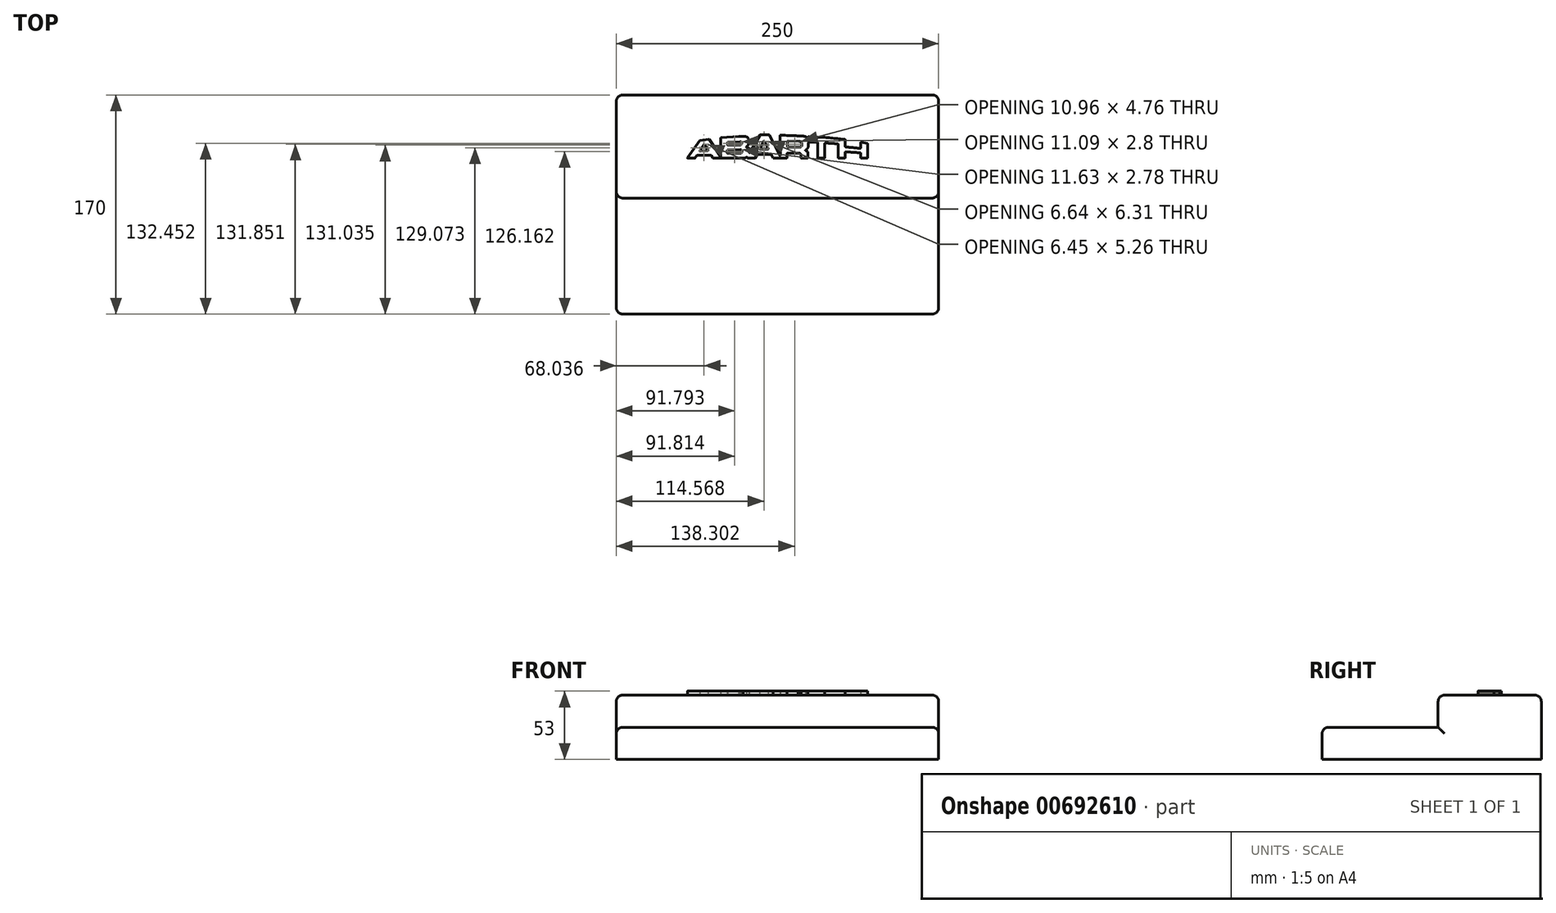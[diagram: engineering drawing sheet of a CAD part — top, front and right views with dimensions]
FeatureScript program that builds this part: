
annotation { "Feature Type Name" : "Feature", "Feature Type Description" : "" }
export const myFeature = defineFeature(function(context is Context, id is Id, definition is map)
    precondition{}
    {
        {
            var Q0;
            Q0=qCreatedBy(makeId("Top.planeOp"),FACE);
            var sketch = newSketch(context, id + "F0", { "sketchPlane" : qUnion([Q0])});
            skLineSegment(sketch, "E0.bottom", {"start": v(125, -40) * mm, "end": v(-125, -40) * mm});
            skLineSegment(sketch, "E0.top", {"start": v(125, 40) * mm, "end": v(-125, 40) * mm});
            skLineSegment(sketch, "E0.left", {"start": v(125, -40) * mm, "end": v(125, 40) * mm});
            skLineSegment(sketch, "E0.right", {"start": v(-125, -40) * mm, "end": v(-125, 40) * mm});
            skPoint(sketch, "E0.middle", {"position": v(0, 0) * mm});
            skSolve(sketch);
        }
        {
            var Q0;
            Q0=makeQuery(id+"F0.imprint","IMPRINT",FACE,{"disambiguationData":[TD([[makeQuery(id+"F0.imprint","IMPRINT",EDGE,{"derivedFrom":sQuery(id+"F0.wireOp",EDGE,"E0.bottom")}),-1.0]])]});
            extrude(context, id + "F1", {"entities" : qUnion([Q0]), "depth" : 25 * mm, "offsetDistance" : 25 * mm});
        }
        {
            var Q0;
            Q0=makeQuery(id+"F1.opExtrude","CAP_FACE",FACE,{"disambiguationData":[OSD([sQuery(id+"F0.wireOp",EDGE,"E0.bottom"),sQuery(id+"F0.wireOp",EDGE,"E0.top"),sQuery(id+"F0.wireOp",EDGE,"E0.left"),sQuery(id+"F0.wireOp",EDGE,"E0.right")])],"isStart":false});
            var sketch = newSketch(context, id + "F2", { "sketchPlane" : qUnion([Q0])});
            skLineSegment(sketch, "E1", {"start": v(-69.64, -9.06) * mm, "end": v(-64.06, -9.06) * mm});
            skLineSegment(sketch, "E2", {"start": v(-63.89, -8.97) * mm, "end": v(-62.5, -6.84) * mm});
            skLineSegment(sketch, "E3", {"start": v(-62.33, -6.75) * mm, "end": v(-51.48, -6.75) * mm});
            skLineSegment(sketch, "E4", {"start": v(-51.3, -6.84) * mm, "end": v(-50.02, -8.94) * mm});
            skLineSegment(sketch, "E5", {"start": v(-49.85, -9.04) * mm, "end": v(-26.5, -9) * mm});
            skLineSegment(sketch, "E6", {"start": v(-23.3, -8.96) * mm, "end": v(-17.46, -9.05) * mm});
            skLineSegment(sketch, "E7", {"start": v(-17.28, -8.95) * mm, "end": v(-15.84, -6.3) * mm});
            skLineSegment(sketch, "E8", {"start": v(-15.75, -6.24) * mm, "end": v(-4.93, -6.24) * mm});
            skLineSegment(sketch, "E9", {"start": v(-4.75, -6.35) * mm, "end": v(-3.41, -9) * mm});
            skLineSegment(sketch, "E10", {"start": v(-3.41, -9) * mm, "end": v(7.3, -8.99) * mm});
            skLineSegment(sketch, "E11", {"start": v(7.5, -8.79) * mm, "end": v(7.49, -5.27) * mm});
            skLineSegment(sketch, "E12", {"start": v(7.69, -5.07) * mm, "end": v(15.94, -5.07) * mm});
            skLineSegment(sketch, "E13", {"start": v(18.18, -6.73) * mm, "end": v(18.18, -8.82) * mm});
            skLineSegment(sketch, "E14", {"start": v(18.38, -9.02) * mm, "end": v(23.46, -9.02) * mm});
            skLineSegment(sketch, "E15", {"start": v(23.66, -8.82) * mm, "end": v(23.66, -5.07) * mm});
            skLineSegment(sketch, "E16", {"start": v(31.26, 3.12) * mm, "end": v(31.26, -8.71) * mm});
            skLineSegment(sketch, "E17", {"start": v(31.46, -8.91) * mm, "end": v(36.56, -8.91) * mm});
            skLineSegment(sketch, "E18", {"start": v(36.76, -8.71) * mm, "end": v(36.76, 2.47) * mm});
            skLineSegment(sketch, "E19", {"start": v(47.1, 1.82) * mm, "end": v(47.11, -8.74) * mm});
            skLineSegment(sketch, "E20", {"start": v(47.31, -8.94) * mm, "end": v(52.37, -8.94) * mm});
            skLineSegment(sketch, "E21", {"start": v(52.57, -8.74) * mm, "end": v(52.57, -4.38) * mm});
            skLineSegment(sketch, "E22", {"start": v(64.52, -5.17) * mm, "end": v(64.53, -8.78) * mm});
            skLineSegment(sketch, "E23", {"start": v(64.73, -8.98) * mm, "end": v(69.68, -8.98) * mm});
            skLineSegment(sketch, "E24", {"start": v(69.88, -8.78) * mm, "end": v(69.88, 2.26) * mm});
            skLineSegment(sketch, "E25", {"start": v(69.7, 2.46) * mm, "end": v(64.77, 3.25) * mm});
            skLineSegment(sketch, "E26", {"start": v(64.54, 3.05) * mm, "end": v(64.54, -1.3) * mm});
            skLineSegment(sketch, "E27", {"start": v(52.64, -0.15) * mm, "end": v(52.64, 5.27) * mm});
            skPoint(sketch, "E28.1.internal.snap0", {"position": v(58.57, -0.93) * mm});
            skFitSpline(sketch, "E28", {"points": [v(52.75, -0.34) * mm, v(59.5, -0.93) * mm, v(64.4, -1.5) * mm], "startDerivative": vector(13.02, -1.03) * mm, "endDerivative": vector(10.2, -1.3) * mm});
            skFitSpline(sketch, "E29", {"points": [v(64.42, -4.98) * mm, v(60.34, -4.58) * mm, v(55.98, -4.34) * mm, v(52.7, -4.18) * mm], "startDerivative": vector(-11.7, 1.26) * mm, "endDerivative": vector(-10.29, 0.51) * mm});
            skFitSpline(sketch, "E30", {"points": [v(36.88, 2.68) * mm, v(42.24, 2.46) * mm, v(47, 2.01) * mm], "startDerivative": vector(10.58, -0.3) * mm, "endDerivative": vector(9.64, -1.04) * mm});
            skFitSpline(sketch, "E31", {"points": [v(52.52, 5.46) * mm, v(38.45, 6.9) * mm, v(23.98, 7.7) * mm], "startDerivative": vector(-28.22, 3.11) * mm, "endDerivative": vector(-28.88, 1.38) * mm});
            skLineSegment(sketch, "E32", {"start": v(24.28, 3.32) * mm, "end": v(31.06, 3.32) * mm});
            skLineSegment(sketch, "E33", {"start": v(-6.23, 8.9) * mm, "end": v(1.9, -7.08) * mm});
            skLineSegment(sketch, "E34", {"start": v(2.07, 8.37) * mm, "end": v(2.27, -6.99) * mm});
            skLineSegment(sketch, "E35", {"start": v(-13.5, 9.02) * mm, "end": v(-6.4, 9) * mm});
            skLineSegment(sketch, "E36", {"start": v(-13.68, 8.92) * mm, "end": v(-21.48, -4.95) * mm});
            skLineSegment(sketch, "E37", {"start": v(-69.8, -8.74) * mm, "end": v(-60.27, 4.59) * mm});
            skLineSegment(sketch, "E38", {"start": v(-60.13, 4.67) * mm, "end": v(-53.17, 5.56) * mm});
            skLineSegment(sketch, "E39", {"start": v(-52.98, 5.47) * mm, "end": v(-44.42, -7.51) * mm});
            skLineSegment(sketch, "E40", {"start": v(-44.05, -7.4) * mm, "end": v(-44.05, 6.67) * mm});
            skLineSegment(sketch, "E41", {"start": v(-43.87, 6.87) * mm, "end": v(-30.13, 7.83) * mm});
            skLineSegment(sketch, "E42", {"start": v(-23.5, -8.77) * mm, "end": v(-23.5, -8.37) * mm});
            skFitSpline(sketch, "E43", {"points": [v(-23.7, -8.13) * mm, v(-24.5, -8.62) * mm, v(-25.52, -8.94) * mm, v(-26.5, -9) * mm], "startDerivative": vector(-2.31, -1.62) * mm, "endDerivative": vector(-2.91, -0.1) * mm});
            skFitSpline(sketch, "E44", {"points": [v(-21.67, -5.2) * mm, v(-21.66, -3.24) * mm, v(-21.74, -2.03) * mm, v(-22.12, -1.33) * mm, v(-23.2, -0.73) * mm, v(-24.06, -0.6) * mm], "startDerivative": vector(0.06, 7.93) * mm, "endDerivative": vector(-4.73, 0.3) * mm});
            skFitSpline(sketch, "E45", {"points": [v(-24.13, -0.1) * mm, v(-23.14, 0.54) * mm, v(-22.14, 2.46) * mm, v(-22.12, 4.53) * mm, v(-22.65, 6.42) * mm, v(-23.83, 7.5) * mm, v(-25.3, 7.9) * mm, v(-28.37, 7.93) * mm, v(-30.13, 7.83) * mm], "startDerivative": vector(10.17, 4.79) * mm, "endDerivative": vector(-13.04, -0.76) * mm});
            skFitSpline(sketch, "E46", {"points": [v(2.4, 8.78) * mm, v(16.04, 8.3) * mm, v(20.13, 8.07) * mm, v(22.39, 7.37) * mm, v(23.23, 6.73) * mm, v(23.65, 6.14) * mm], "startDerivative": vector(38.58, -1.46) * mm, "endDerivative": vector(4.08, -6.44) * mm});
            skFitSpline(sketch, "E47", {"points": [v(24.08, 3.2) * mm, v(24, 0.71) * mm, v(23.66, -0.8) * mm, v(22.61, -2.27) * mm, v(21.75, -2.78) * mm], "startDerivative": vector(-0.22, -8.68) * mm, "endDerivative": vector(-4.38, -1.91) * mm});
            skFitSpline(sketch, "E48", {"points": [v(18.18, -6.73) * mm, v(18.07, -5.9) * mm, v(17.47, -5.26) * mm, v(16.6, -5.1) * mm, v(15.94, -5.07) * mm], "startDerivative": vector(0, 3.34) * mm, "endDerivative": vector(-2.8, 0.11) * mm});
            skFitSpline(sketch, "E49", {"points": [v(23.66, -5.07) * mm, v(23.6, -4.53) * mm, v(23.33, -4) * mm, v(22.8, -3.56) * mm, v(22, -3.3) * mm, v(21.8, -3.27) * mm], "startDerivative": vector(-0.2, 2.72) * mm, "endDerivative": vector(-1.34, 0.14) * mm});
            skLineSegment(sketch, "E50", {"start": v(23.85, 7.5) * mm, "end": v(23.88, 6.47) * mm});
            skArc(sketch, "E51.filletArc", {"start": v(-69.8, -8.74) * mm, "mid": v(-69.82, -8.95) * mm, "end": v(-69.64, -9.06) * mm});
            skArc(sketch, "E52.filletArc", {"start": v(-64.06, -9.06) * mm, "mid": v(-63.96, -9.03) * mm, "end": v(-63.89, -8.97) * mm});
            skArc(sketch, "E53.filletArc", {"start": v(-62.33, -6.75) * mm, "mid": v(-62.42, -6.77) * mm, "end": v(-62.5, -6.84) * mm});
            skArc(sketch, "E54.filletArc", {"start": v(-51.3, -6.84) * mm, "mid": v(-51.38, -6.77) * mm, "end": v(-51.48, -6.75) * mm});
            skArc(sketch, "E55.filletArc", {"start": v(-50.02, -8.94) * mm, "mid": v(-49.95, -9.01) * mm, "end": v(-49.85, -9.04) * mm});
            skArc(sketch, "E56.filletArc", {"start": v(-52.98, 5.47) * mm, "mid": v(-53.06, 5.54) * mm, "end": v(-53.17, 5.56) * mm});
            skPoint(sketch, "E57.visualSharp", {"position": v(-60.22, 4.66) * mm});
            skArc(sketch, "E57.filletArc", {"start": v(-60.13, 4.67) * mm, "mid": v(-60.2, 4.64) * mm, "end": v(-60.27, 4.59) * mm});
            skArc(sketch, "E58.filletArc", {"start": v(-43.87, 6.87) * mm, "mid": v(-44, 6.8) * mm, "end": v(-44.05, 6.67) * mm});
            skArc(sketch, "E59.filletArc", {"start": v(-17.46, -9.05) * mm, "mid": v(-17.36, -9.02) * mm, "end": v(-17.28, -8.95) * mm});
            skArc(sketch, "E60.filletArc", {"start": v(-23.5, -8.77) * mm, "mid": v(-23.44, -8.9) * mm, "end": v(-23.3, -8.96) * mm});
            skArc(sketch, "E61.filletArc", {"start": v(-15.75, -6.24) * mm, "mid": v(-15.8, -6.25) * mm, "end": v(-15.84, -6.3) * mm});
            skArc(sketch, "E62.filletArc", {"start": v(-4.75, -6.35) * mm, "mid": v(-4.82, -6.27) * mm, "end": v(-4.93, -6.24) * mm});
            skArc(sketch, "E63.filletArc", {"start": v(7.3, -8.99) * mm, "mid": v(7.44, -8.93) * mm, "end": v(7.5, -8.79) * mm});
            skArc(sketch, "E64.filletArc", {"start": v(7.69, -5.07) * mm, "mid": v(7.55, -5.13) * mm, "end": v(7.49, -5.27) * mm});
            skArc(sketch, "E65.filletArc", {"start": v(18.18, -8.82) * mm, "mid": v(18.24, -8.96) * mm, "end": v(18.38, -9.02) * mm});
            skArc(sketch, "E66.filletArc", {"start": v(23.46, -9.02) * mm, "mid": v(23.6, -8.96) * mm, "end": v(23.66, -8.82) * mm});
            skArc(sketch, "E67.filletArc", {"start": v(24.28, 3.32) * mm, "mid": v(24.14, 3.26) * mm, "end": v(24.08, 3.12) * mm});
            skArc(sketch, "E68.filletArc", {"start": v(31.26, 3.12) * mm, "mid": v(31.2, 3.26) * mm, "end": v(31.06, 3.32) * mm});
            skArc(sketch, "E69.filletArc", {"start": v(31.26, -8.71) * mm, "mid": v(31.32, -8.85) * mm, "end": v(31.46, -8.91) * mm});
            skArc(sketch, "E70.filletArc", {"start": v(36.56, -8.91) * mm, "mid": v(36.7, -8.85) * mm, "end": v(36.76, -8.71) * mm});
            skArc(sketch, "E71.filletArc", {"start": v(36.96, 2.67) * mm, "mid": v(36.82, 2.62) * mm, "end": v(36.76, 2.47) * mm});
            skArc(sketch, "E72.filletArc", {"start": v(47.1, 1.82) * mm, "mid": v(47.05, 1.95) * mm, "end": v(46.93, 2.02) * mm});
            skArc(sketch, "E73.filletArc", {"start": v(47.11, -8.74) * mm, "mid": v(47.17, -8.89) * mm, "end": v(47.31, -8.94) * mm});
            skArc(sketch, "E74.filletArc", {"start": v(52.37, -8.94) * mm, "mid": v(52.51, -8.89) * mm, "end": v(52.57, -8.74) * mm});
            skArc(sketch, "E75.filletArc", {"start": v(52.78, -4.18) * mm, "mid": v(52.64, -4.24) * mm, "end": v(52.57, -4.38) * mm});
            skArc(sketch, "E76.filletArc", {"start": v(64.53, -8.78) * mm, "mid": v(64.59, -8.92) * mm, "end": v(64.73, -8.98) * mm});
            skArc(sketch, "E77.filletArc", {"start": v(64.52, -5.17) * mm, "mid": v(64.47, -5.04) * mm, "end": v(64.35, -4.97) * mm});
            skArc(sketch, "E78.filletArc", {"start": v(69.68, -8.98) * mm, "mid": v(69.82, -8.92) * mm, "end": v(69.88, -8.78) * mm});
            skArc(sketch, "E79.filletArc", {"start": v(69.88, 2.26) * mm, "mid": v(69.83, 2.39) * mm, "end": v(69.7, 2.46) * mm});
            skArc(sketch, "E80.filletArc", {"start": v(64.77, 3.25) * mm, "mid": v(64.6, 3.2) * mm, "end": v(64.54, 3.05) * mm});
            skArc(sketch, "E81.filletArc", {"start": v(64.31, -1.5) * mm, "mid": v(64.47, -1.45) * mm, "end": v(64.54, -1.3) * mm});
            skArc(sketch, "E82.filletArc", {"start": v(52.64, -0.15) * mm, "mid": v(52.69, -0.29) * mm, "end": v(52.82, -0.35) * mm});
            skArc(sketch, "E83.filletArc", {"start": v(52.64, 5.27) * mm, "mid": v(52.59, 5.4) * mm, "end": v(52.46, 5.47) * mm});
            skArc(sketch, "E84.filletArc", {"start": v(24.06, 7.7) * mm, "mid": v(23.9, 7.65) * mm, "end": v(23.85, 7.5) * mm});
            skArc(sketch, "E85.filletArc", {"start": v(2.48, 8.78) * mm, "mid": v(2.19, 8.66) * mm, "end": v(2.07, 8.37) * mm});
            skPoint(sketch, "E86.visualSharp", {"position": v(-6.28, 9) * mm});
            skArc(sketch, "E86.filletArc", {"start": v(-6.23, 8.9) * mm, "mid": v(-6.3, 8.97) * mm, "end": v(-6.4, 9) * mm});
            skArc(sketch, "E87.filletArc", {"start": v(-13.5, 9.02) * mm, "mid": v(-13.6, 9) * mm, "end": v(-13.68, 8.92) * mm});
            skArc(sketch, "E88.filletArc", {"start": v(-44.42, -7.51) * mm, "mid": v(-44.2, -7.6) * mm, "end": v(-44.05, -7.4) * mm});
            skArc(sketch, "E89.filletArc", {"start": v(-21.67, -4.9) * mm, "mid": v(-21.6, -5) * mm, "end": v(-21.48, -4.95) * mm});
            skArc(sketch, "E90.filletArc", {"start": v(1.9, -7.08) * mm, "mid": v(2.12, -7.18) * mm, "end": v(2.27, -6.99) * mm});
            skArc(sketch, "E91.filletArc", {"start": v(-23.5, -8.37) * mm, "mid": v(-23.61, -8.2) * mm, "end": v(-23.82, -8.2) * mm});
            skArc(sketch, "E92.filletArc", {"start": v(23.51, 6.35) * mm, "mid": v(23.74, 6.27) * mm, "end": v(23.88, 6.47) * mm});
            skArc(sketch, "E93.filletArc", {"start": v(-23.93, -0.01) * mm, "mid": v(-24.1, -0.36) * mm, "end": v(-23.82, -0.61) * mm});
            skArc(sketch, "E94.filletArc", {"start": v(21.93, -2.7) * mm, "mid": v(21.75, -3.02) * mm, "end": v(22, -3.3) * mm});
            skLineSegment(sketch, "E95", {"start": v(-59.98, -3.56) * mm, "end": v(-53.93, -3.28) * mm});
            skLineSegment(sketch, "E96", {"start": v(-53.77, -2.97) * mm, "end": v(-56.66, 1.61) * mm});
            skLineSegment(sketch, "E97", {"start": v(-57, 1.61) * mm, "end": v(-60.16, -3.25) * mm});
            skLineSegment(sketch, "E98", {"start": v(-13.55, -2.12) * mm, "end": v(-7.31, -2.12) * mm});
            skLineSegment(sketch, "E99", {"start": v(-7.14, -1.83) * mm, "end": v(-10.08, 4.08) * mm});
            skLineSegment(sketch, "E100", {"start": v(-10.43, 4.09) * mm, "end": v(-13.72, -1.82) * mm});
            skLineSegment(sketch, "E101", {"start": v(7.82, 4.03) * mm, "end": v(7.82, -0.23) * mm});
            skLineSegment(sketch, "E102", {"start": v(8.02, -0.43) * mm, "end": v(16.64, -0.53) * mm});
            skLineSegment(sketch, "E103", {"start": v(16.49, 4.03) * mm, "end": v(8.03, 4.23) * mm});
            skLineSegment(sketch, "E104", {"start": v(18.78, 2.1) * mm, "end": v(18.78, 0.85) * mm});
            skFitSpline(sketch, "E105", {"points": [v(16.49, 4.03) * mm, v(17.65, 3.85) * mm, v(18.44, 3.3) * mm, v(18.76, 2.56) * mm, v(18.78, 2.1) * mm], "startDerivative": vector(4.08, -0.25) * mm, "endDerivative": vector(-0.06, -2.33) * mm});
            skFitSpline(sketch, "E106", {"points": [v(18.78, 0.85) * mm, v(18.75, 0.44) * mm, v(18.34, -0.14) * mm, v(17.52, -0.48) * mm, v(16.64, -0.53) * mm], "startDerivative": vector(0.06, -2.04) * mm, "endDerivative": vector(-3.14, 0) * mm});
            skLineSegment(sketch, "E107", {"start": v(-38.67, 3.2) * mm, "end": v(-38.75, 1.26) * mm});
            skLineSegment(sketch, "E108", {"start": v(-38.48, 3.4) * mm, "end": v(-29.2, 3.85) * mm});
            skLineSegment(sketch, "E109", {"start": v(-29.17, 1.19) * mm, "end": v(-38.55, 1.05) * mm});
            skLineSegment(sketch, "E110", {"start": v(-28.93, -2.45) * mm, "end": v(-38.73, -2.79) * mm});
            skLineSegment(sketch, "E111", {"start": v(-28.99, -5.23) * mm, "end": v(-38.8, -5.21) * mm});
            skFitSpline(sketch, "E112", {"points": [v(-29.2, 3.85) * mm, v(-28.27, 3.74) * mm, v(-27.78, 3.28) * mm, v(-27.64, 2.65) * mm, v(-27.8, 1.95) * mm, v(-28.19, 1.46) * mm, v(-28.54, 1.24) * mm, v(-28.87, 1.19) * mm, v(-29.17, 1.19) * mm], "startDerivative": vector(6.28, 0.05) * mm, "endDerivative": vector(-3.3, 0.32) * mm});
            skFitSpline(sketch, "E113", {"points": [v(-28.99, -5.23) * mm, v(-28.29, -5.18) * mm, v(-27.72, -4.7) * mm, v(-27.37, -3.67) * mm, v(-27.75, -2.83) * mm, v(-28.4, -2.5) * mm, v(-28.93, -2.45) * mm], "startDerivative": vector(4.62, -0.21) * mm, "endDerivative": vector(-3.8, 0.08) * mm});
            skLineSegment(sketch, "E114.trimOffspring", {"start": v(-38.92, -2.98) * mm, "end": v(-39, -5) * mm});
            skPoint(sketch, "E115.visualSharp", {"position": v(-56.82, 1.87) * mm});
            skArc(sketch, "E115.filletArc", {"start": v(-56.66, 1.61) * mm, "mid": v(-56.82, 1.7) * mm, "end": v(-57, 1.61) * mm});
            skPoint(sketch, "E116.visualSharp", {"position": v(-53.58, -3.26) * mm});
            skArc(sketch, "E116.filletArc", {"start": v(-53.93, -3.28) * mm, "mid": v(-53.76, -3.17) * mm, "end": v(-53.77, -2.97) * mm});
            skPoint(sketch, "E117.visualSharp", {"position": v(-60.37, -3.58) * mm});
            skArc(sketch, "E117.filletArc", {"start": v(-60.16, -3.25) * mm, "mid": v(-60.16, -3.46) * mm, "end": v(-59.98, -3.56) * mm});
            skPoint(sketch, "E118.visualSharp", {"position": v(-10.25, 4.42) * mm});
            skArc(sketch, "E118.filletArc", {"start": v(-10.08, 4.08) * mm, "mid": v(-10.25, 4.19) * mm, "end": v(-10.43, 4.09) * mm});
            skPoint(sketch, "E119.visualSharp", {"position": v(-13.9, -2.12) * mm});
            skArc(sketch, "E119.filletArc", {"start": v(-13.72, -1.82) * mm, "mid": v(-13.72, -2.02) * mm, "end": v(-13.55, -2.12) * mm});
            skPoint(sketch, "E120.visualSharp", {"position": v(-7, -2.12) * mm});
            skArc(sketch, "E120.filletArc", {"start": v(-7.31, -2.12) * mm, "mid": v(-7.14, -2.02) * mm, "end": v(-7.14, -1.83) * mm});
            skPoint(sketch, "E121.visualSharp", {"position": v(7.82, 4.24) * mm});
            skArc(sketch, "E121.filletArc", {"start": v(8.03, 4.23) * mm, "mid": v(7.88, 4.17) * mm, "end": v(7.82, 4.03) * mm});
            skPoint(sketch, "E122.visualSharp", {"position": v(7.82, -0.42) * mm});
            skArc(sketch, "E122.filletArc", {"start": v(7.82, -0.23) * mm, "mid": v(7.88, -0.37) * mm, "end": v(8.02, -0.43) * mm});
            skPoint(sketch, "E123.visualSharp", {"position": v(-38.67, 3.4) * mm});
            skArc(sketch, "E123.filletArc", {"start": v(-38.48, 3.4) * mm, "mid": v(-38.61, 3.34) * mm, "end": v(-38.67, 3.2) * mm});
            skPoint(sketch, "E124.visualSharp", {"position": v(-38.76, 1.05) * mm});
            skArc(sketch, "E124.filletArc", {"start": v(-38.75, 1.26) * mm, "mid": v(-38.7, 1.12) * mm, "end": v(-38.55, 1.05) * mm});
            skPoint(sketch, "E125.visualSharp", {"position": v(-38.91, -2.8) * mm});
            skArc(sketch, "E125.filletArc", {"start": v(-38.73, -2.79) * mm, "mid": v(-38.86, -2.84) * mm, "end": v(-38.92, -2.98) * mm});
            skPoint(sketch, "E126.visualSharp", {"position": v(-39, -5.21) * mm});
            skArc(sketch, "E126.filletArc", {"start": v(-39, -5) * mm, "mid": v(-38.94, -5.15) * mm, "end": v(-38.8, -5.21) * mm});
            skLineSegment(sketch, "E127", {"start": v(-81, 0) * mm, "end": v(81, 0) * mm, "construction": true});
            skLineSegment(sketch, "E128", {"start": v(0, 13.76) * mm, "end": v(0, -13.76) * mm, "construction": true});
            skPoint(sketch, "E129.middle", {"position": v(0, 0) * mm});
            skSolve(sketch);
        }
        {
            var Q0;
            Q0=qSketchRegion(id+"F2",true);
            extrude(context, id + "F3", {"entities" : qUnion([Q0]), "depth" : 3 * mm, "offsetDistance" : 25 * mm});
        }
        {
            var Q0;
            Q0=makeQuery(id+"F1.opExtrude","CAP_FACE",FACE,{"disambiguationData":[OSD([sQuery(id+"F0.wireOp",EDGE,"E0.bottom"),sQuery(id+"F0.wireOp",EDGE,"E0.top"),sQuery(id+"F0.wireOp",EDGE,"E0.left"),sQuery(id+"F0.wireOp",EDGE,"E0.right")])],"isStart":true});
            var sketch = newSketch(context, id + "F4", { "sketchPlane" : qUnion([Q0])});
            skLineSegment(sketch, "E130.bottom", {"start": v(-125, -40) * mm, "end": v(125, -40) * mm});
            skLineSegment(sketch, "E130.top", {"start": v(-125, 130) * mm, "end": v(125, 130) * mm});
            skLineSegment(sketch, "E130.left", {"start": v(-125, -40) * mm, "end": v(-125, 130) * mm});
            skLineSegment(sketch, "E130.right", {"start": v(125, -40) * mm, "end": v(125, 130) * mm});
            skSolve(sketch);
        }
        {
            var Q0;
            {var subQ0=sQuery(id+"F4.wireOp",EDGE,"E130.top");Q0=makeQuery(id+"F4.imprint","IMPRINT",FACE,{"disambiguationData":[TD([[makeQuery(id+"F4.imprint","IMPRINT",EDGE,{"derivedFrom":subQ0}),-1.0]])]});}
            var Q1;
            {var subQ0=sQuery(id+"F4.wireOp",EDGE,"E130.bottom");Q1=makeQuery(id+"F4.imprint","IMPRINT",FACE,{"disambiguationData":[TD([[makeQuery(id+"F4.imprint","IMPRINT",EDGE,{"derivedFrom":subQ0}),-1.0]])]});}
            extrude(context, id + "F5", {"entities" : qUnion([Q0, Q1]), "operationType" : NewBodyOperationType.ADD, "depth" : 25 * mm, "offsetDistance" : 25 * mm});
        }
        {
            var Q0;
            Q0=makeQuery(id+"F1.opExtrude","CAP_EDGE",EDGE,{"disambiguationData":[OSD([sQuery(id+"F0.wireOp",EDGE,"E0.bottom")])],"isStart":false});
            var Q1;
            Q1=makeQuery(id+"F1.opExtrude","CAP_EDGE",EDGE,{"disambiguationData":[OSD([sQuery(id+"F0.wireOp",EDGE,"E0.left")])],"isStart":false});
            var Q2;
            Q2=makeQuery(id+"F1.opExtrude","CAP_EDGE",EDGE,{"disambiguationData":[OSD([sQuery(id+"F0.wireOp",EDGE,"E0.right")])],"isStart":false});
            var Q3;
            Q3=makeQuery(id+"F1.opExtrude","CAP_EDGE",EDGE,{"disambiguationData":[OSD([sQuery(id+"F0.wireOp",EDGE,"E0.top")])],"isStart":false});
            var Q4;
            Q4=makeQuery(id+"F5.boolean.opBoolean","MERGE",EDGE,{"derivedFrom":[makeQuery(id+"F1.opExtrude","SWEPT_EDGE",EDGE,{"disambiguationData":[OSD([sQuery(id+"F0.wireOp",EDGE,"E0.top"),sQuery(id+"F0.wireOp",EDGE,"E0.left")])]}),makeQuery(id+"F5.opExtrude","SWEPT_EDGE",EDGE,{"disambiguationData":[OSD([sQuery(id+"F4.wireOp",EDGE,"E130.bottom"),sQuery(id+"F4.wireOp",EDGE,"E130.right")])]})]});
            var Q5;
            Q5=makeQuery(id+"F1.opExtrude","SWEPT_EDGE",EDGE,{"disambiguationData":[OSD([sQuery(id+"F0.wireOp",EDGE,"E0.bottom"),sQuery(id+"F0.wireOp",EDGE,"E0.left")])]});
            var Q6;
            Q6=makeQuery(id+"F5.opExtrude","CAP_EDGE",EDGE,{"disambiguationData":[OSD([sQuery(id+"F4.wireOp",EDGE,"E130.right")])],"isStart":true});
            var Q7;
            Q7=makeQuery(id+"F1.opExtrude","SWEPT_EDGE",EDGE,{"disambiguationData":[OSD([sQuery(id+"F0.wireOp",EDGE,"E0.bottom"),sQuery(id+"F0.wireOp",EDGE,"E0.right")])]});
            var Q8;
            Q8=makeQuery(id+"F5.opExtrude","CAP_EDGE",EDGE,{"disambiguationData":[OSD([sQuery(id+"F4.wireOp",EDGE,"E130.left")])],"isStart":true});
            var Q9;
            Q9=makeQuery(id+"F5.boolean.opBoolean","MERGE",EDGE,{"derivedFrom":[makeQuery(id+"F1.opExtrude","SWEPT_EDGE",EDGE,{"disambiguationData":[OSD([sQuery(id+"F0.wireOp",EDGE,"E0.top"),sQuery(id+"F0.wireOp",EDGE,"E0.right")])]}),makeQuery(id+"F5.opExtrude","SWEPT_EDGE",EDGE,{"disambiguationData":[OSD([sQuery(id+"F4.wireOp",EDGE,"E130.bottom"),sQuery(id+"F4.wireOp",EDGE,"E130.left")])]})]});
            var Q10;
            Q10=makeQuery(id+"F5.opExtrude","SWEPT_EDGE",EDGE,{"disambiguationData":[OSD([sQuery(id+"F4.wireOp",EDGE,"E130.top"),sQuery(id+"F4.wireOp",EDGE,"E130.left")])]});
            var Q11;
            Q11=makeQuery(id+"F5.opExtrude","CAP_EDGE",EDGE,{"disambiguationData":[OSD([sQuery(id+"F4.wireOp",EDGE,"E130.top")])],"isStart":true});
            var Q12;
            Q12=makeQuery(id+"F5.opExtrude","SWEPT_EDGE",EDGE,{"disambiguationData":[OSD([sQuery(id+"F4.wireOp",EDGE,"E130.top"),sQuery(id+"F4.wireOp",EDGE,"E130.right")])]});
            fillet(context, id + "F6", {"entities" : qUnion([Q0, Q1, Q2, Q3, Q4, Q5, Q6, Q7, Q8, Q9, Q10, Q11, Q12]), "radius" : 5 * mm, "tangentPropagation" : true, "allowEdgeOverflow" : false});
        }
    });
